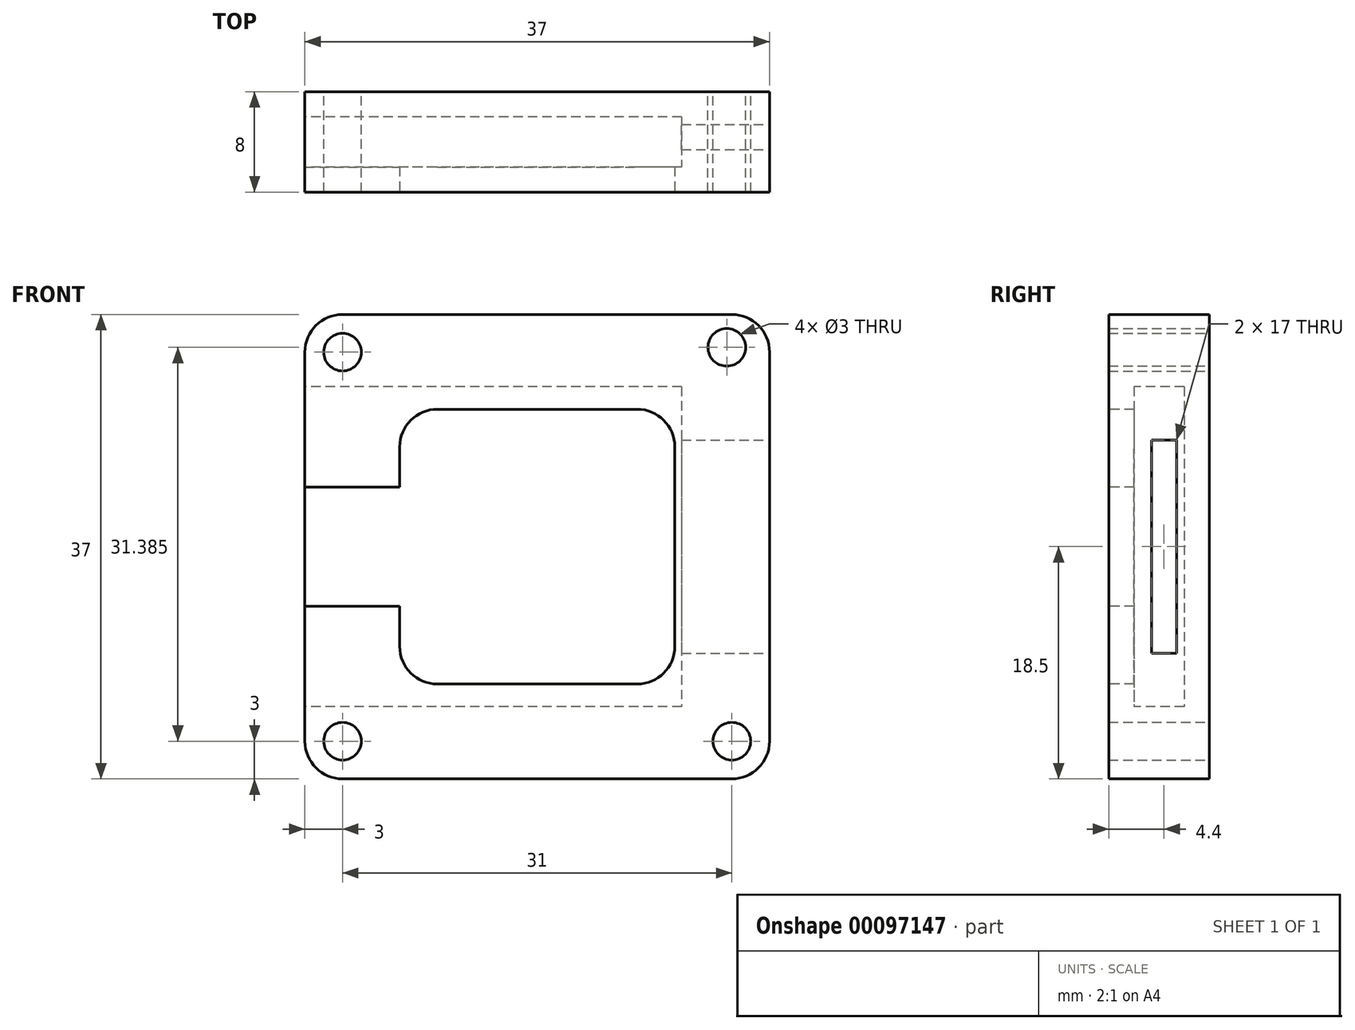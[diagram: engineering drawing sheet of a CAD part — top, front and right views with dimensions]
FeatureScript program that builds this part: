
annotation { "Feature Type Name" : "Feature", "Feature Type Description" : "" }
export const myFeature = defineFeature(function(context is Context, id is Id, definition is map)
    precondition{}
    {
        {
            var Q0;
            Q0=qCreatedBy(makeId("Front.planeOp"),FACE);
            var sketch = newSketch(context, id + "F0", { "sketchPlane" : qUnion([Q0])});
            skLineSegment(sketch, "E0.bottom", {"start": v(-15.5, 18.5) * mm, "end": v(15.5, 18.5) * mm});
            skLineSegment(sketch, "E0.top", {"start": v(-15.5, -18.5) * mm, "end": v(15.5, -18.5) * mm});
            skLineSegment(sketch, "E0.left", {"start": v(-18.5, 15.5) * mm, "end": v(-18.5, -15.5) * mm});
            skLineSegment(sketch, "E0.right", {"start": v(18.5, 15.5) * mm, "end": v(18.5, -15.5) * mm});
            skPoint(sketch, "E0.middle", {"position": v(0, 0) * mm});
            skPoint(sketch, "E1.visualSharp", {"position": v(18.5, 18.5) * mm});
            skArc(sketch, "E1.filletArc", {"start": v(18.5, 15.5) * mm, "mid": v(17.62, 17.62) * mm, "end": v(15.5, 18.5) * mm});
            skPoint(sketch, "E2.visualSharp", {"position": v(18.5, -18.5) * mm});
            skArc(sketch, "E2.filletArc", {"start": v(15.5, -18.5) * mm, "mid": v(17.62, -17.62) * mm, "end": v(18.5, -15.5) * mm});
            skPoint(sketch, "E3.visualSharp", {"position": v(-18.5, -18.5) * mm});
            skArc(sketch, "E3.filletArc", {"start": v(-18.5, -15.5) * mm, "mid": v(-17.62, -17.62) * mm, "end": v(-15.5, -18.5) * mm});
            skPoint(sketch, "E4.visualSharp", {"position": v(-18.5, 18.5) * mm});
            skArc(sketch, "E4.filletArc", {"start": v(-15.5, 18.5) * mm, "mid": v(-17.62, 17.62) * mm, "end": v(-18.5, 15.5) * mm});
            skCircle(sketch, "E5", {"center": v(-15.5, 15.5) * mm, "radius": 1.5 * mm});
            skCircle(sketch, "E6", {"center": v(15.1, 15.89) * mm, "radius": 1.5 * mm});
            skCircle(sketch, "E7", {"center": v(15.5, -15.5) * mm, "radius": 1.5 * mm});
            skCircle(sketch, "E8", {"center": v(-15.5, -15.5) * mm, "radius": 1.5 * mm});
            skSolve(sketch);
        }
        {
            var Q0;
            Q0=makeQuery(id+"F0.imprint","IMPRINT",FACE,{"disambiguationData":[TD([[makeQuery(id+"F0.imprint","IMPRINT",EDGE,{"derivedFrom":sQuery(id+"F0.wireOp",EDGE,"E0.bottom")}),-1.0]])]});
            extrude(context, id + "F1", {"entities" : qUnion([Q0]), "depth" : 8 * mm});
        }
        {
            var Q0;
            Q0=makeQuery(id+"F1.opExtrude","CAP_FACE",FACE,{"disambiguationData":[OSD([sQuery(id+"F0.wireOp",EDGE,"E0.bottom"),sQuery(id+"F0.wireOp",EDGE,"E0.top"),sQuery(id+"F0.wireOp",EDGE,"E0.left"),sQuery(id+"F0.wireOp",EDGE,"E0.right"),sQuery(id+"F0.wireOp",EDGE,"E1.filletArc"),sQuery(id+"F0.wireOp",EDGE,"E2.filletArc"),sQuery(id+"F0.wireOp",EDGE,"E3.filletArc"),sQuery(id+"F0.wireOp",EDGE,"E4.filletArc"),sQuery(id+"F0.wireOp",EDGE,"E5"),sQuery(id+"F0.wireOp",EDGE,"E6"),sQuery(id+"F0.wireOp",EDGE,"E7"),sQuery(id+"F0.wireOp",EDGE,"E8")])],"isStart":false});
            var sketch = newSketch(context, id + "F2", { "sketchPlane" : qUnion([Q0])});
            skLineSegment(sketch, "E9.bottom", {"start": v(-7.95, -10.95) * mm, "end": v(7.95, -10.95) * mm});
            skLineSegment(sketch, "E9.top", {"start": v(-7.95, 10.95) * mm, "end": v(7.95, 10.95) * mm});
            skLineSegment(sketch, "E9.left", {"start": v(-10.95, -7.95) * mm, "end": v(-10.95, 7.95) * mm});
            skLineSegment(sketch, "E9.right", {"start": v(10.95, -7.95) * mm, "end": v(10.95, 7.95) * mm});
            skPoint(sketch, "E9.middle", {"position": v(0, 0) * mm});
            skPoint(sketch, "E10.visualSharp", {"position": v(-10.95, -10.95) * mm});
            skArc(sketch, "E10.filletArc", {"start": v(-10.95, -7.95) * mm, "mid": v(-10.07, -10.07) * mm, "end": v(-7.95, -10.95) * mm});
            skPoint(sketch, "E11.visualSharp", {"position": v(-10.95, 10.95) * mm});
            skArc(sketch, "E11.filletArc", {"start": v(-7.95, 10.95) * mm, "mid": v(-10.07, 10.07) * mm, "end": v(-10.95, 7.95) * mm});
            skPoint(sketch, "E12.visualSharp", {"position": v(10.95, 10.95) * mm});
            skArc(sketch, "E12.filletArc", {"start": v(10.95, 7.95) * mm, "mid": v(10.07, 10.07) * mm, "end": v(7.95, 10.95) * mm});
            skPoint(sketch, "E13.visualSharp", {"position": v(10.95, -10.95) * mm});
            skArc(sketch, "E13.filletArc", {"start": v(7.95, -10.95) * mm, "mid": v(10.07, -10.07) * mm, "end": v(10.95, -7.95) * mm});
            skLineSegment(sketch, "E14.bottom", {"start": v(-18.5, -4.73) * mm, "end": v(-3.4, -4.73) * mm});
            skLineSegment(sketch, "E14.top", {"start": v(-18.5, 4.73) * mm, "end": v(-3.4, 4.73) * mm});
            skLineSegment(sketch, "E14.left", {"start": v(-18.5, -4.73) * mm, "end": v(-18.5, 4.73) * mm});
            skLineSegment(sketch, "E14.right", {"start": v(-3.4, -4.73) * mm, "end": v(-3.4, 4.73) * mm});
            skPoint(sketch, "E14.middle", {"position": v(-10.95, 0) * mm});
            skSolve(sketch);
        }
        {
            var Q0;
            Q0 = qSketchRegion(id + "F2", true);
            extrude(context, id + "F3", {"entities" : qUnion([Q0]), "operationType" : NewBodyOperationType.REMOVE, "oppositeDirection" : true, "depth" : 6 * mm});
        }
        {
            var Q0;
            Q0=makeQuery(id+"F1.opExtrude","SWEPT_FACE",FACE,{"disambiguationData":[OSD([sQuery(id+"F0.wireOp",EDGE,"E0.right")])]});
            var sketch = newSketch(context, id + "F4", { "sketchPlane" : qUnion([Q0])});
            skLineSegment(sketch, "E15", {"start": v(0, 0) * mm, "end": v(-3.6, 0) * mm});
            skLineSegment(sketch, "E16.bottom", {"start": v(-4.6, 8.5) * mm, "end": v(-2.6, 8.5) * mm});
            skLineSegment(sketch, "E16.top", {"start": v(-4.6, -8.5) * mm, "end": v(-2.6, -8.5) * mm});
            skLineSegment(sketch, "E16.left", {"start": v(-4.6, 8.5) * mm, "end": v(-4.6, -8.5) * mm});
            skLineSegment(sketch, "E16.right", {"start": v(-2.6, 8.5) * mm, "end": v(-2.6, -8.5) * mm});
            skPoint(sketch, "E16.middle", {"position": v(-3.6, 0) * mm});
            skSolve(sketch);
        }
        {
            var Q0;
            {var subQ1=sQuery(id+"F4.wireOp",EDGE,"E16.bottom");Q0=makeQuery(id+"F4.imprint","IMPRINT",FACE,{"disambiguationData":[TD([[makeQuery(id+"F4.imprint","IMPRINT",EDGE,{"derivedFrom":subQ1}),-1.0]])]});}
            extrude(context, id + "F5", {"entities" : qUnion([Q0]), "operationType" : NewBodyOperationType.REMOVE, "oppositeDirection" : true, "depth" : 8 * mm});
        }
        {
            var Q0;
            Q0=makeQuery(id+"F1.opExtrude","SWEPT_FACE",FACE,{"disambiguationData":[OSD([sQuery(id+"F0.wireOp",EDGE,"E0.left")])]});
            var sketch = newSketch(context, id + "F6", { "sketchPlane" : qUnion([Q0])});
            skLineSegment(sketch, "E17", {"start": v(0, 0) * mm, "end": v(4, 0) * mm});
            skPoint(sketch, "E17.endSnap0", {"position": v(2, 0) * mm});
            skLineSegment(sketch, "E18.bottom", {"start": v(2, 12.75) * mm, "end": v(6, 12.75) * mm});
            skLineSegment(sketch, "E18.top", {"start": v(2, -12.75) * mm, "end": v(6, -12.75) * mm});
            skLineSegment(sketch, "E18.left", {"start": v(2, 12.75) * mm, "end": v(2, -12.75) * mm});
            skLineSegment(sketch, "E18.right", {"start": v(6, 12.75) * mm, "end": v(6, -12.75) * mm});
            skPoint(sketch, "E18.middle", {"position": v(4, 0) * mm});
            skSolve(sketch);
        }
        {
            var Q0;
            {var subQ0=sQuery(id+"F6.wireOp",EDGE,"E18.bottom");Q0=makeQuery(id+"F6.imprint","IMPRINT",FACE,{"disambiguationData":[TD([[makeQuery(id+"F6.imprint","IMPRINT",EDGE,{"derivedFrom":subQ0}),-1.0]])]});}
            var Q1;
            {var subQ0=sQuery(id+"F6.wireOp",EDGE,"E18.top");Q1=makeQuery(id+"F6.imprint","IMPRINT",FACE,{"disambiguationData":[TD([[makeQuery(id+"F6.imprint","IMPRINT",EDGE,{"derivedFrom":subQ0}),1.0]])]});}
            var Q2;
            {var subQ0=sQuery(id+"F6.wireOp",EDGE,"E18.left");var subQ9=makeQuery(id+"F6.imprint","INTERSECT",VERTEX,{"derivedFrom":[sQuery(id+"F6.wireOp",EDGE,"E17"),subQ0]});Q2=makeQuery(id+"F6.imprint","IMPRINT",FACE,{"disambiguationData":[TD([[makeQuery(id+"F6.imprint","IMPRINT",EDGE,{"disambiguationData":[TD([[subQ9,1.0]])],"derivedFrom":subQ0}),1.0]])]});}
            extrude(context, id + "F7", {"entities" : qUnion([Q0, Q1, Q2]), "operationType" : NewBodyOperationType.REMOVE, "oppositeDirection" : true, "depth" : 30 * mm});
        }
    });
